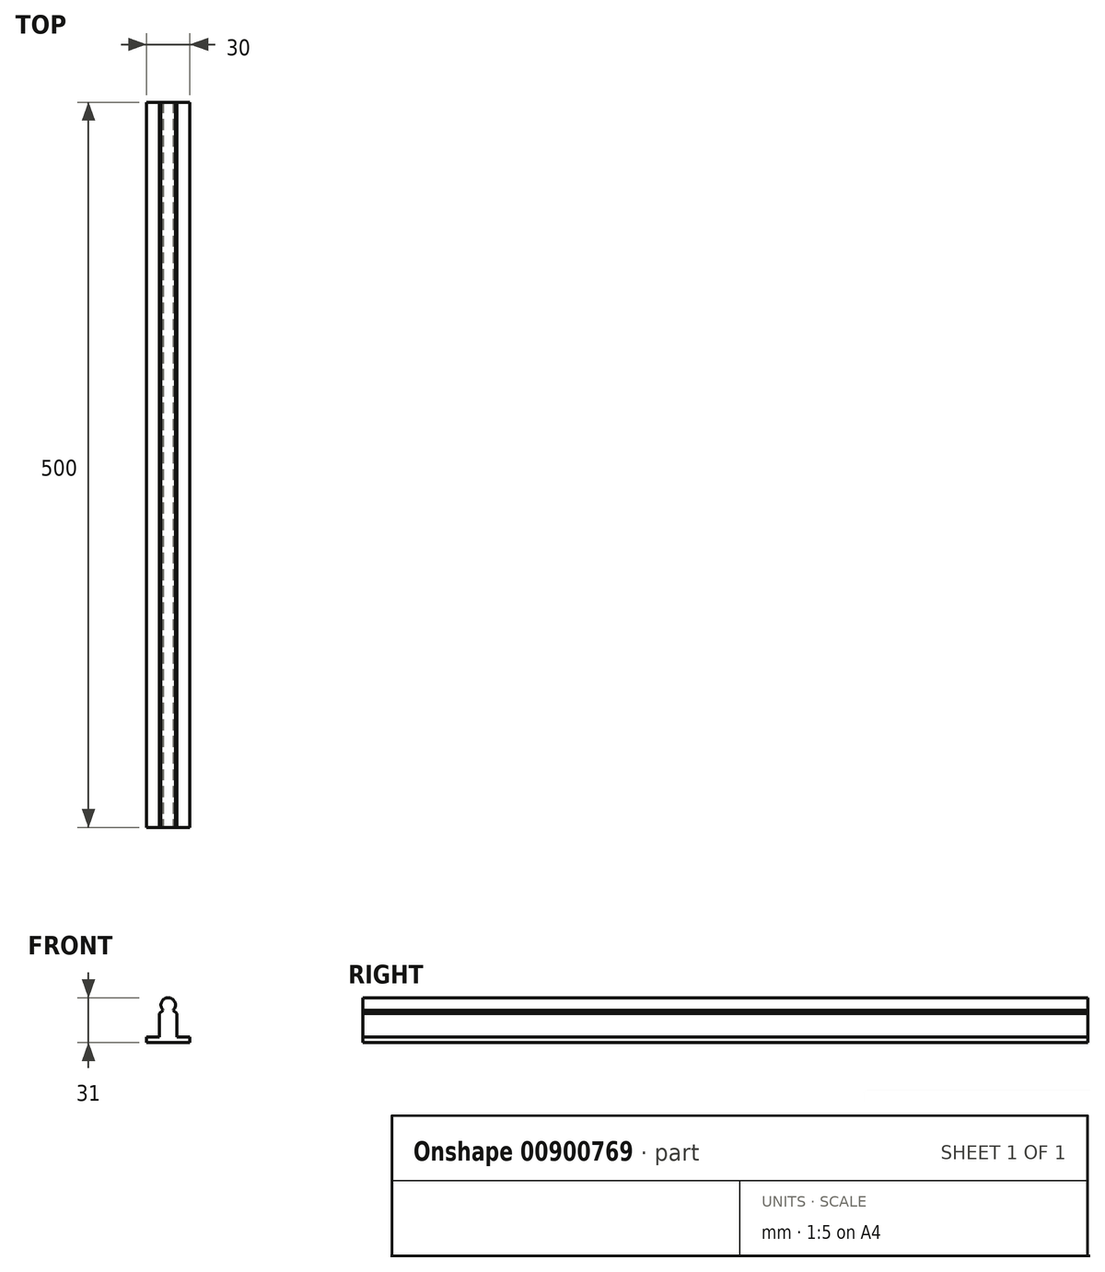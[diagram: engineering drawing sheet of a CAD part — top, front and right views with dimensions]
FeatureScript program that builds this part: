
annotation { "Feature Type Name" : "Feature", "Feature Type Description" : "" }
export const myFeature = defineFeature(function(context is Context, id is Id, definition is map)
    precondition{}
    {
        {
            var Q0;
            Q0=qCreatedBy(makeId("Front.planeOp"),FACE);
            var sketch = newSketch(context, id + "F0", { "sketchPlane" : qUnion([Q0])});
            skCircle(sketch, "E0", {"center": v(0, 0) * mm, "radius": 5 * mm});
            skLineSegment(sketch, "E1.bottom", {"start": v(-15, -26) * mm, "end": v(15, -26) * mm});
            skLineSegment(sketch, "E1.left", {"start": v(-15, -26) * mm, "end": v(-15, -22) * mm});
            skLineSegment(sketch, "E1.right", {"start": v(15, -26) * mm, "end": v(15, -22) * mm});
            skLineSegment(sketch, "E2", {"start": v(0, 0) * mm, "end": v(0, -26) * mm});
            skLineSegment(sketch, "E3", {"start": v(-15, -22) * mm, "end": v(15, -22) * mm});
            skLineSegment(sketch, "E4", {"start": v(0, 0) * mm, "end": v(-6, -6) * mm});
            skLineSegment(sketch, "E5", {"start": v(-6, -6) * mm, "end": v(-6, -22) * mm});
            skLineSegment(sketch, "E6", {"start": v(-6, -22) * mm, "end": v(0, -22) * mm});
            skLineSegment(sketch, "E7", {"start": v(0, -22) * mm, "end": v(6, -22) * mm});
            skLineSegment(sketch, "E8", {"start": v(6, -22) * mm, "end": v(6, -6) * mm});
            skLineSegment(sketch, "E9", {"start": v(6, -6) * mm, "end": v(0, 0) * mm});
            skSolve(sketch);
        }
        {
            var Q0;
            Q0 = qSketchRegion(id + "F0", true);
            extrude(context, id + "F1", {"entities" : qUnion([Q0]), "oppositeDirection" : true, "depth" : 500 * mm, "offsetDistance" : 25 * mm});
        }
    });
